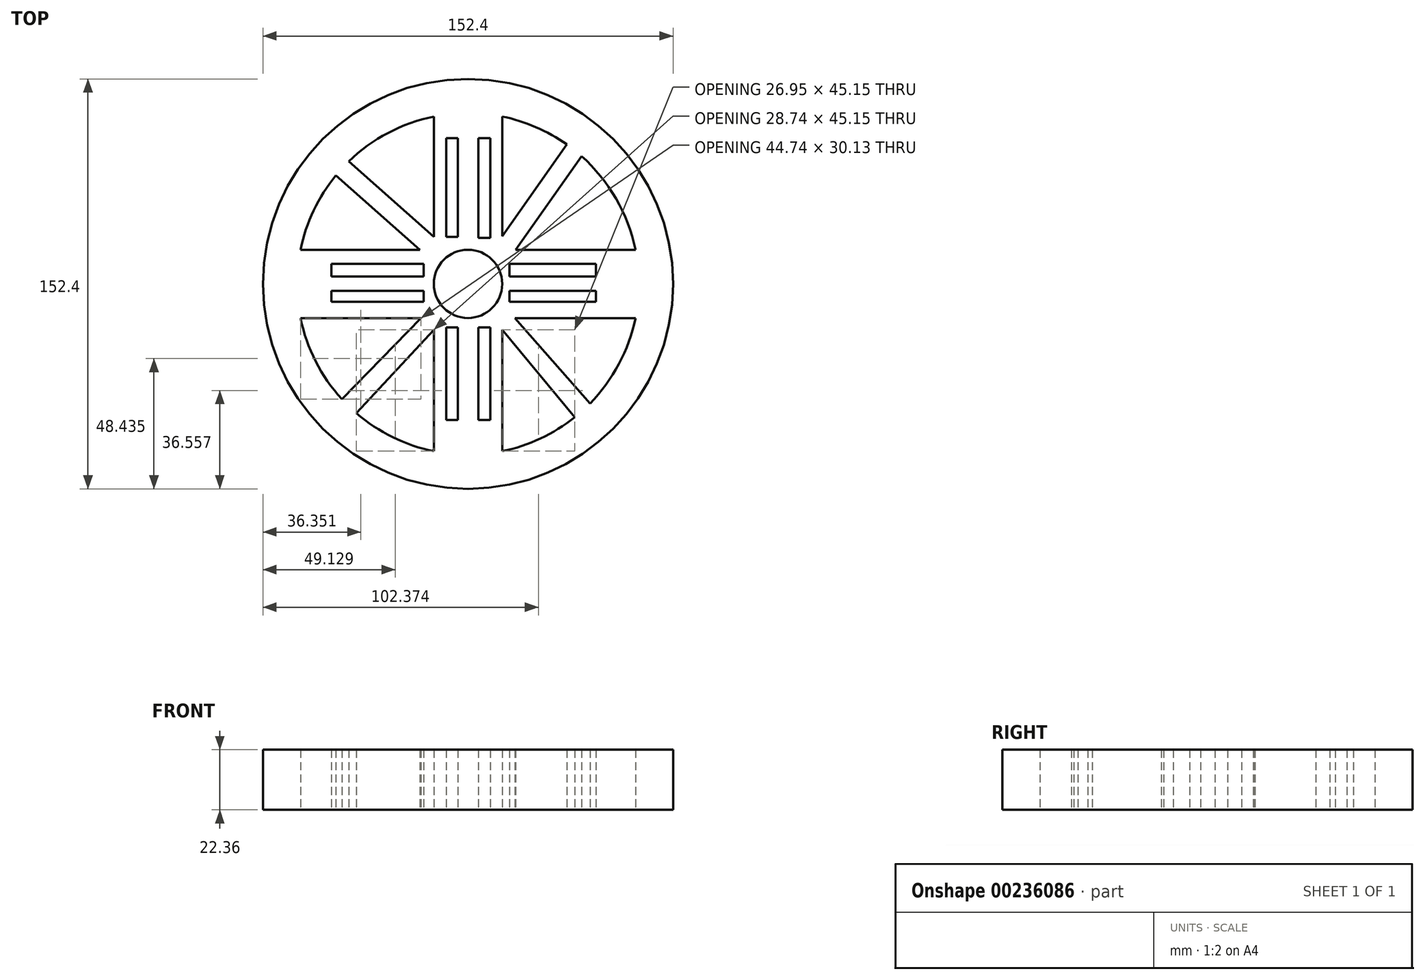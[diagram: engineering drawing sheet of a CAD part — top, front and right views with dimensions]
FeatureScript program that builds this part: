
annotation { "Feature Type Name" : "Feature", "Feature Type Description" : "" }
export const myFeature = defineFeature(function(context is Context, id is Id, definition is map)
    precondition{}
    {
        {
            var Q0;
            Q0=qCreatedBy(makeId("Top.planeOp"),FACE);
            var sketch = newSketch(context, id + "F0", { "sketchPlane" : qUnion([Q0])});
            skCircle(sketch, "E0", {"center": v(0, 0) * mm, "radius": 12.7 * mm});
            skArc(sketch, "E1", {"start": v(-12.7, 62.22) * mm, "mid": v(-29.71, 56.12) * mm, "end": v(-44.32, 45.48) * mm});
            skCircle(sketch, "E2", {"center": v(0, 0) * mm, "radius": 76.2 * mm});
            skLineSegment(sketch, "E3", {"start": v(0, 0) * mm, "end": v(0, 76.2) * mm});
            skLineSegment(sketch, "E4.0", {"start": v(12.7, 12.7) * mm, "end": v(12.7, 62.22) * mm});
            skLineSegment(sketch, "E5.0", {"start": v(-12.7, 12.7) * mm, "end": v(-12.7, 62.22) * mm});
            skLineSegment(sketch, "E6", {"start": v(0, 0) * mm, "end": v(0, -76.2) * mm});
            skLineSegment(sketch, "E7", {"start": v(0, 0) * mm, "end": v(-76.2, 0) * mm});
            skLineSegment(sketch, "E8", {"start": v(0, 0) * mm, "end": v(76.2, 0) * mm});
            skLineSegment(sketch, "E9.0", {"start": v(-12.7, -12.7) * mm, "end": v(-62.22, -12.7) * mm});
            skLineSegment(sketch, "E10.0", {"start": v(-12.7, 12.7) * mm, "end": v(-62.22, 12.7) * mm});
            skLineSegment(sketch, "E11.0", {"start": v(-12.7, -12.7) * mm, "end": v(-12.7, -62.22) * mm});
            skLineSegment(sketch, "E12.0", {"start": v(12.7, -12.7) * mm, "end": v(12.7, -62.22) * mm});
            skLineSegment(sketch, "E13.0", {"start": v(12.7, -12.7) * mm, "end": v(62.22, -12.7) * mm});
            skLineSegment(sketch, "E14.0", {"start": v(12.7, 12.7) * mm, "end": v(62.22, 12.7) * mm});
            skArc(sketch, "E15.trimOffspring", {"start": v(62.22, 12.7) * mm, "mid": v(55.02, 31.7) * mm, "end": v(42.18, 47.47) * mm});
            skArc(sketch, "E16.trimOffspring", {"start": v(-62.22, -12.7) * mm, "mid": v(-56.6, -28.8) * mm, "end": v(-46.88, -42.83) * mm});
            skLineSegment(sketch, "E17.bottom", {"start": v(-8.1, 54.2) * mm, "end": v(-3.83, 54.2) * mm});
            skLineSegment(sketch, "E17.top", {"start": v(-8.1, 17.5) * mm, "end": v(-3.83, 17.5) * mm});
            skLineSegment(sketch, "E17.left", {"start": v(-8.1, 54.2) * mm, "end": v(-8.1, 17.5) * mm});
            skLineSegment(sketch, "E17.right", {"start": v(-3.83, 54.2) * mm, "end": v(-3.83, 17.5) * mm});
            skLineSegment(sketch, "E18.bottom", {"start": v(3.86, 17.07) * mm, "end": v(8.34, 17.07) * mm});
            skLineSegment(sketch, "E18.top", {"start": v(3.86, 54.2) * mm, "end": v(8.34, 54.2) * mm});
            skLineSegment(sketch, "E18.left", {"start": v(3.86, 17.07) * mm, "end": v(3.86, 54.2) * mm});
            skLineSegment(sketch, "E18.right", {"start": v(8.34, 17.07) * mm, "end": v(8.34, 54.2) * mm});
            skLineSegment(sketch, "E19.bottom", {"start": v(-3.83, -16.22) * mm, "end": v(-8.1, -16.22) * mm});
            skLineSegment(sketch, "E19.top", {"start": v(-3.83, -50.57) * mm, "end": v(-8.1, -50.57) * mm});
            skLineSegment(sketch, "E19.left", {"start": v(-3.83, -16.22) * mm, "end": v(-3.83, -50.57) * mm});
            skLineSegment(sketch, "E19.right", {"start": v(-8.1, -16.22) * mm, "end": v(-8.1, -50.57) * mm});
            skLineSegment(sketch, "E20.bottom", {"start": v(3.86, -16.22) * mm, "end": v(8.34, -16.22) * mm});
            skLineSegment(sketch, "E20.top", {"start": v(3.86, -50.57) * mm, "end": v(8.34, -50.57) * mm});
            skLineSegment(sketch, "E20.left", {"start": v(3.86, -16.22) * mm, "end": v(3.86, -50.57) * mm});
            skLineSegment(sketch, "E20.right", {"start": v(8.34, -16.22) * mm, "end": v(8.34, -50.57) * mm});
            skLineSegment(sketch, "E21.bottom", {"start": v(15.38, -2.56) * mm, "end": v(47.6, -2.56) * mm});
            skLineSegment(sketch, "E21.top", {"start": v(15.38, -6.61) * mm, "end": v(47.6, -6.61) * mm});
            skLineSegment(sketch, "E21.left", {"start": v(15.38, -2.56) * mm, "end": v(15.38, -6.61) * mm});
            skLineSegment(sketch, "E21.right", {"start": v(47.6, -2.56) * mm, "end": v(47.6, -6.61) * mm});
            skLineSegment(sketch, "E22.bottom", {"start": v(-16.41, -6.61) * mm, "end": v(-50.76, -6.61) * mm});
            skLineSegment(sketch, "E22.top", {"start": v(-16.41, -2.56) * mm, "end": v(-50.76, -2.56) * mm});
            skLineSegment(sketch, "E22.left", {"start": v(-16.41, -6.61) * mm, "end": v(-16.41, -2.56) * mm});
            skLineSegment(sketch, "E22.right", {"start": v(-50.76, -6.61) * mm, "end": v(-50.76, -2.56) * mm});
            skLineSegment(sketch, "E23.bottom", {"start": v(-50.76, 7.47) * mm, "end": v(-16.41, 7.47) * mm});
            skLineSegment(sketch, "E23.top", {"start": v(-50.76, 2.77) * mm, "end": v(-16.41, 2.77) * mm});
            skLineSegment(sketch, "E23.left", {"start": v(-50.76, 7.47) * mm, "end": v(-50.76, 2.77) * mm});
            skLineSegment(sketch, "E23.right", {"start": v(-16.41, 7.47) * mm, "end": v(-16.41, 2.77) * mm});
            skLineSegment(sketch, "E24.bottom", {"start": v(15.38, 2.77) * mm, "end": v(47.6, 2.77) * mm});
            skLineSegment(sketch, "E24.top", {"start": v(15.38, 7.47) * mm, "end": v(47.6, 7.47) * mm});
            skLineSegment(sketch, "E24.left", {"start": v(15.38, 2.77) * mm, "end": v(15.38, 7.47) * mm});
            skLineSegment(sketch, "E24.right", {"start": v(47.6, 2.77) * mm, "end": v(47.6, 7.47) * mm});
            skLineSegment(sketch, "E25", {"start": v(12.7, 17.7) * mm, "end": v(36.7, 51.82) * mm});
            skLineSegment(sketch, "E26", {"start": v(17.72, 12.7) * mm, "end": v(42.18, 47.47) * mm});
            skLineSegment(sketch, "E27", {"start": v(-17.9, 12.7) * mm, "end": v(-49.08, 40.29) * mm});
            skLineSegment(sketch, "E28", {"start": v(-12.7, 17.5) * mm, "end": v(-44.32, 45.48) * mm});
            skLineSegment(sketch, "E29", {"start": v(-17.48, -12.7) * mm, "end": v(-46.88, -42.83) * mm});
            skLineSegment(sketch, "E30", {"start": v(-12.7, -17.07) * mm, "end": v(-41.44, -48.11) * mm});
            skLineSegment(sketch, "E31", {"start": v(12.7, -17.07) * mm, "end": v(39.65, -49.6) * mm});
            skLineSegment(sketch, "E32", {"start": v(17.51, -12.7) * mm, "end": v(45.32, -44.48) * mm});
            skArc(sketch, "E33.trimOffspring", {"start": v(45.32, -44.48) * mm, "mid": v(56.07, -29.81) * mm, "end": v(62.22, -12.7) * mm});
            skArc(sketch, "E34.trimOffspring", {"start": v(12.7, -62.22) * mm, "mid": v(26.92, -57.5) * mm, "end": v(39.65, -49.6) * mm});
            skArc(sketch, "E35.trimOffspring", {"start": v(-41.44, -48.11) * mm, "mid": v(-27.97, -57) * mm, "end": v(-12.7, -62.22) * mm});
            skArc(sketch, "E36.trimOffspring", {"start": v(-49.08, 40.29) * mm, "mid": v(-57.33, 27.3) * mm, "end": v(-62.22, 12.7) * mm});
            skArc(sketch, "E37.trimOffspring", {"start": v(36.7, 51.82) * mm, "mid": v(25.24, 58.27) * mm, "end": v(12.7, 62.22) * mm});
            skSolve(sketch);
        }
        {
            var Q0;
            {var subQ9=sQuery(id+"F0.wireOp",EDGE,"E1");Q0=makeQuery(id+"F0.imprint","IMPRINT",FACE,{"disambiguationData":[TD([[makeQuery(id+"F0.imprint","IMPRINT",EDGE,{"derivedFrom":subQ9}),-1.0]])]});}
            var Q1;
            {var subQ0=sQuery(id+"F0.wireOp",EDGE,"E15.trimOffspring");Q1=makeQuery(id+"F0.imprint","IMPRINT",FACE,{"disambiguationData":[TD([[makeQuery(id+"F0.imprint","IMPRINT",EDGE,{"derivedFrom":subQ0}),-1.0]])]});}
            var Q2;
            Q2=makeQuery(id+"F0.imprint","IMPRINT",FACE,{"disambiguationData":[TD([[makeQuery(id+"F0.imprint","IMPRINT",EDGE,{"derivedFrom":sQuery(id+"F0.wireOp",EDGE,"E20.bottom")}),1.0]])]});
            var Q3;
            {var subQ1=sQuery(id+"F0.wireOp",EDGE,"E16.trimOffspring");Q3=makeQuery(id+"F0.imprint","IMPRINT",FACE,{"disambiguationData":[TD([[makeQuery(id+"F0.imprint","IMPRINT",EDGE,{"derivedFrom":subQ1}),-1.0]])]});}
            extrude(context, id + "F1", {"entities" : qUnion([Q0, Q1, Q2, Q3]), "endBound" : BoundingType.SYMMETRIC, "depth" : 22.35 * mm});
        }
    });
